# Revit family: TYCO-FPP-FireClass-FC410MIM MINI INPUT MODULE
name_source: partatom
category: Electrical Fixtures
revit_build: Autodesk Revit 2014 (Build: 20130308_1515(x64)
units: mm (PartAtom-declared; Revit-internal decimal feet)

## types (1)
- TYCO-FPP-FireClass-FC410MIM MINI INPUT MODULE
    Alarm State Current = 2.8mA
    COVER = Cap
    Description = Mini Contact Module
    EOL Resistor Value = 200 Ohms
    Keynote = The remote LED (if required, not supplied) must be located within
the same electrical enclosure.
    Length = 48 mm
    Loop Voltage = 20V to 40Vdc
    Manufacturer = Tyco
    Max. MIM800 / Loop2 = 200/250
200/250
    Model = FireClass- 555.800.701
    Monitor Resistor Value = 100 Ohms
    Operating Temperature = - 25 - + 70 ºC
    PCB = PCB
    Quiescent Current = 275μA (typical)
    Relative Humidity = 10% to 95%
    Storage Temperature = –40°C to +80°C
    Thickness = 13 mm
    Type Comments = The FC410MIM Mini Input module is designed to monitor fire contacts, such as
extinguishing system control, ventilation control, fire door control etc.
    URL = https://fireclass.co.uk
    Weight = 22g
    Width = 57 mm

## geometry (parser evidence)
native form markers: Sweep x1
no freeform markers — native parametric forms only
